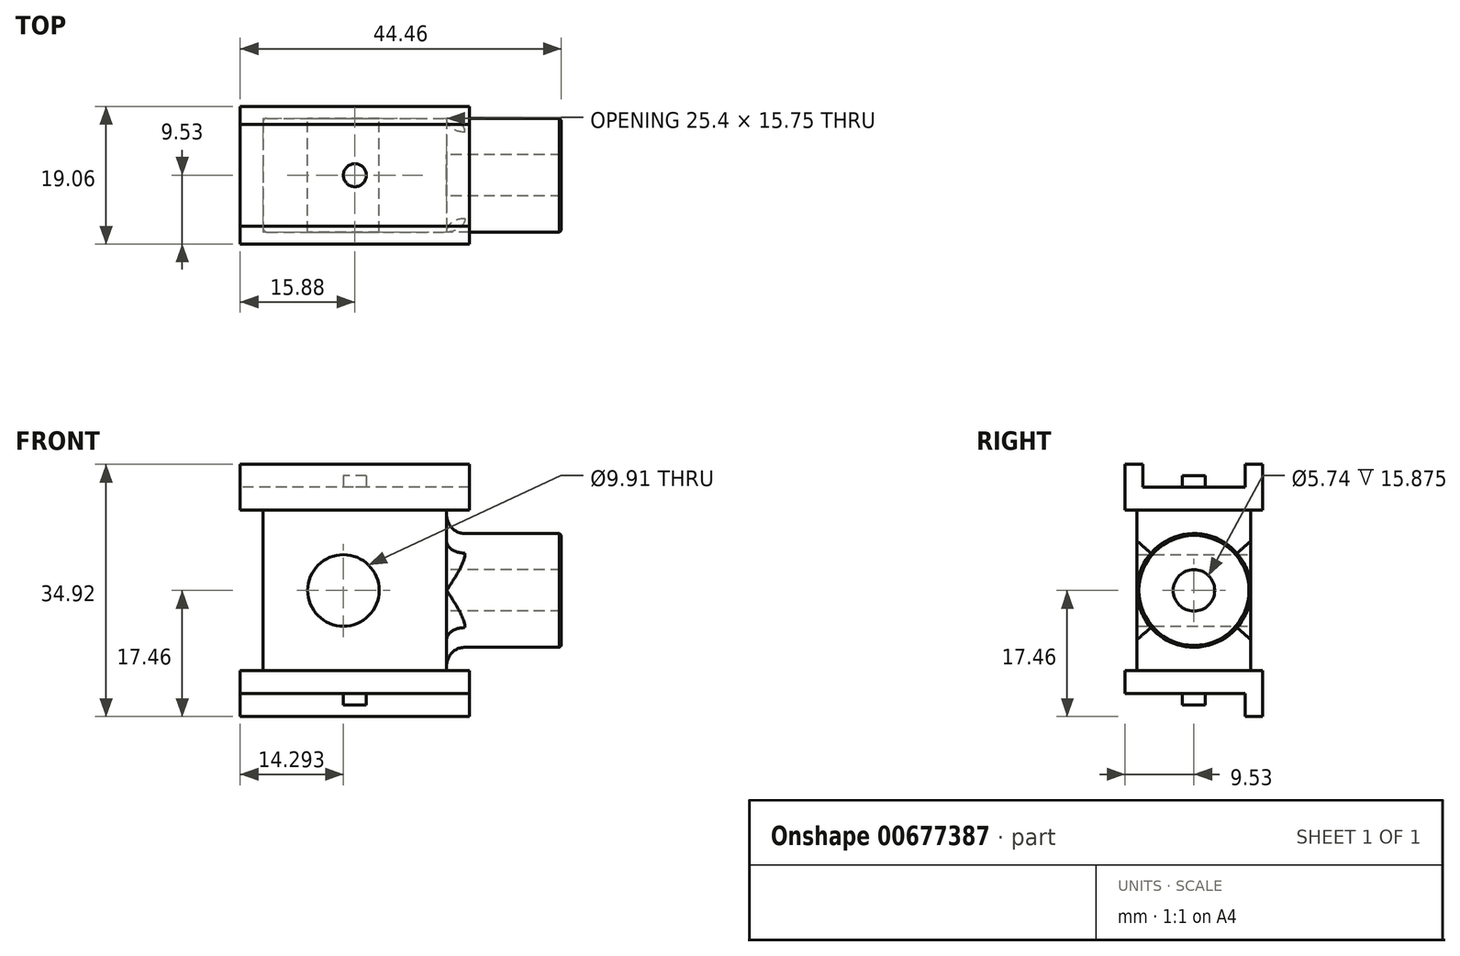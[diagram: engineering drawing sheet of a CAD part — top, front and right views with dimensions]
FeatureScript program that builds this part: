
annotation { "Feature Type Name" : "Feature", "Feature Type Description" : "" }
export const myFeature = defineFeature(function(context is Context, id is Id, definition is map)
    precondition{}
    {
        {
            var Q0;
            Q0=qCreatedBy(makeId("Top.planeOp"),FACE);
            var sketch = newSketch(context, id + "F0", { "sketchPlane" : qUnion([Q0])});
            skLineSegment(sketch, "E0.bottom", {"start": v(-12.7, 7.87) * mm, "end": v(12.7, 7.87) * mm});
            skLineSegment(sketch, "E0.top", {"start": v(-12.7, -7.87) * mm, "end": v(12.7, -7.87) * mm});
            skLineSegment(sketch, "E0.left", {"start": v(-12.7, 7.87) * mm, "end": v(-12.7, -7.87) * mm});
            skLineSegment(sketch, "E0.right", {"start": v(12.7, 7.87) * mm, "end": v(12.7, -7.87) * mm});
            skPoint(sketch, "E0.middle", {"position": v(0, 0) * mm});
            skSolve(sketch);
        }
        {
            var Q0;
            Q0=makeQuery(id+"F0.imprint","IMPRINT",FACE,{"disambiguationData":[TD([[makeQuery(id+"F0.imprint","IMPRINT",EDGE,{"derivedFrom":sQuery(id+"F0.wireOp",EDGE,"E0.bottom")}),-1.0]])]});
            extrude(context, id + "F1", {"entities" : qUnion([Q0]), "endBound" : BoundingType.SYMMETRIC, "depth" : 22.22 * mm, "offsetDistance" : 25.4 * mm});
        }
        {
            var Q0;
            Q0=makeQuery(id+"F1.opExtrude","CAP_FACE",FACE,{"disambiguationData":[OSD([sQuery(id+"F0.wireOp",EDGE,"E0.bottom"),sQuery(id+"F0.wireOp",EDGE,"E0.top"),sQuery(id+"F0.wireOp",EDGE,"E0.left"),sQuery(id+"F0.wireOp",EDGE,"E0.right")])],"isStart":false});
            var sketch = newSketch(context, id + "F2", { "sketchPlane" : qUnion([Q0])});
            skLineSegment(sketch, "E1.bottom", {"start": v(-15.87, 9.52) * mm, "end": v(15.88, 9.52) * mm});
            skLineSegment(sketch, "E1.top", {"start": v(-15.88, -9.52) * mm, "end": v(15.87, -9.52) * mm});
            skLineSegment(sketch, "E1.left", {"start": v(-15.88, 9.52) * mm, "end": v(-15.88, -9.52) * mm});
            skLineSegment(sketch, "E1.right", {"start": v(15.88, 9.52) * mm, "end": v(15.87, -9.52) * mm});
            skPoint(sketch, "E1.middle", {"position": v(0, 0) * mm});
            skSolve(sketch);
        }
        {
            var Q0;
            Q0=makeQuery(id+"F1.opExtrude","CAP_FACE",FACE,{"disambiguationData":[OSD([sQuery(id+"F0.wireOp",EDGE,"E0.bottom"),sQuery(id+"F0.wireOp",EDGE,"E0.top"),sQuery(id+"F0.wireOp",EDGE,"E0.left"),sQuery(id+"F0.wireOp",EDGE,"E0.right")])],"isStart":true});
            var sketch = newSketch(context, id + "F3", { "sketchPlane" : qUnion([Q0])});
            skLineSegment(sketch, "E2.bottom", {"start": v(15.88, -9.52) * mm, "end": v(-15.88, -9.53) * mm});
            skLineSegment(sketch, "E2.top", {"start": v(15.88, 9.53) * mm, "end": v(-15.88, 9.53) * mm});
            skLineSegment(sketch, "E2.left", {"start": v(15.88, -9.52) * mm, "end": v(15.87, 9.53) * mm});
            skLineSegment(sketch, "E2.right", {"start": v(-15.88, -9.53) * mm, "end": v(-15.88, 9.52) * mm});
            skPoint(sketch, "E2.middle", {"position": v(0, 0) * mm});
            skSolve(sketch);
        }
        {
            var Q0;
            Q0=makeQuery(id+"F2.imprint","IMPRINT",FACE,{"disambiguationData":[TD([[makeQuery(id+"F2.imprint","IMPRINT",EDGE,{"derivedFrom":makeQuery(id+"F1.opExtrude","CAP_EDGE",EDGE,{"disambiguationData":[OSD([sQuery(id+"F0.wireOp",EDGE,"E0.bottom")])],"isStart":false})}),-1.0]])]});
            var Q1;
            Q1=makeQuery(id+"F2.imprint","IMPRINT",FACE,{"disambiguationData":[TD([[makeQuery(id+"F2.imprint","IMPRINT",EDGE,{"derivedFrom":sQuery(id+"F2.wireOp",EDGE,"E1.bottom")}),-1.0]])]});
            extrude(context, id + "F4", {"entities" : qUnion([Q0, Q1]), "operationType" : NewBodyOperationType.ADD, "depth" : 3.17 * mm, "offsetDistance" : 25.4 * mm});
        }
        {
            var Q0;
            Q0=makeQuery(id+"F3.imprint","IMPRINT",FACE,{"disambiguationData":[TD([[makeQuery(id+"F3.imprint","IMPRINT",EDGE,{"derivedFrom":makeQuery(id+"F1.opExtrude","CAP_EDGE",EDGE,{"disambiguationData":[OSD([sQuery(id+"F0.wireOp",EDGE,"E0.bottom")])],"isStart":true})}),1.0]])]});
            var Q1;
            Q1=makeQuery(id+"F3.imprint","IMPRINT",FACE,{"disambiguationData":[TD([[makeQuery(id+"F3.imprint","IMPRINT",EDGE,{"derivedFrom":sQuery(id+"F3.wireOp",EDGE,"E2.bottom")}),-1.0]])]});
            extrude(context, id + "F5", {"entities" : qUnion([Q0, Q1]), "operationType" : NewBodyOperationType.ADD, "depth" : 3.17 * mm, "offsetDistance" : 25.4 * mm});
        }
        {
            var Q0;
            Q0=makeQuery(id+"F5.opExtrude","CAP_FACE",FACE,{"disambiguationData":[OSD([sQuery(id+"F3.wireOp",EDGE,"E2.bottom"),sQuery(id+"F3.wireOp",EDGE,"E2.top"),sQuery(id+"F3.wireOp",EDGE,"E2.left"),sQuery(id+"F3.wireOp",EDGE,"E2.right")])],"isStart":false});
            var sketch = newSketch(context, id + "F6", { "sketchPlane" : qUnion([Q0])});
            skLineSegment(sketch, "E3", {"start": v(-15.88, -9.53) * mm, "end": v(15.88, -9.52) * mm});
            skLineSegment(sketch, "E4", {"start": v(15.88, -9.52) * mm, "end": v(15.88, -7.06) * mm});
            skLineSegment(sketch, "E5", {"start": v(15.88, -7.06) * mm, "end": v(-15.88, -7.06) * mm});
            skLineSegment(sketch, "E6", {"start": v(-15.88, -7.06) * mm, "end": v(-15.88, -9.53) * mm});
            skLineSegment(sketch, "E7", {"start": v(-15.88, 9.52) * mm, "end": v(15.87, 9.53) * mm});
            skLineSegment(sketch, "E8", {"start": v(15.87, 9.53) * mm, "end": v(-15.88, 9.52) * mm});
            skLineSegment(sketch, "E9", {"start": v(-15.88, 7.06) * mm, "end": v(15.88, 7.06) * mm});
            skLineSegment(sketch, "E10", {"start": v(15.88, 7.06) * mm, "end": v(15.88, 9.53) * mm});
            skLineSegment(sketch, "E11", {"start": v(-15.88, 7.06) * mm, "end": v(-15.88, 9.52) * mm});
            skSolve(sketch);
        }
        {
            var Q0;
            Q0=makeQuery(id+"F6.imprint","IMPRINT",FACE,{"disambiguationData":[TD([[makeQuery(id+"F6.imprint","IMPRINT",EDGE,{"derivedFrom":sQuery(id+"F6.wireOp",EDGE,"E3")}),-1.0]])]});
            var Q1;
            Q1=makeQuery(id+"F6.imprint","IMPRINT",FACE,{"disambiguationData":[TD([[makeQuery(id+"F6.imprint","IMPRINT",EDGE,{"derivedFrom":sQuery(id+"F6.wireOp",EDGE,"E8")}),1.0]])]});
            extrude(context, id + "F7", {"entities" : qUnion([Q0, Q1]), "operationType" : NewBodyOperationType.ADD, "depth" : 3.17 * mm, "offsetDistance" : 25.4 * mm});
        }
        {
            var Q0;
            Q0=makeQuery(id+"F4.opExtrude","CAP_FACE",FACE,{"disambiguationData":[OSD([sQuery(id+"F2.wireOp",EDGE,"E1.bottom"),sQuery(id+"F2.wireOp",EDGE,"E1.top"),sQuery(id+"F2.wireOp",EDGE,"E1.left"),sQuery(id+"F2.wireOp",EDGE,"E1.right")])],"isStart":false});
            var sketch = newSketch(context, id + "F8", { "sketchPlane" : qUnion([Q0])});
            skLineSegment(sketch, "E12", {"start": v(15.87, -9.52) * mm, "end": v(-15.88, -9.52) * mm});
            skLineSegment(sketch, "E13", {"start": v(-15.88, -9.52) * mm, "end": v(-15.88, -7.06) * mm});
            skLineSegment(sketch, "E14", {"start": v(-15.88, -7.06) * mm, "end": v(15.87, -7.06) * mm});
            skLineSegment(sketch, "E15", {"start": v(15.88, -7.06) * mm, "end": v(15.88, -9.52) * mm});
            skLineSegment(sketch, "E16", {"start": v(15.88, 9.52) * mm, "end": v(15.88, 7.06) * mm});
            skLineSegment(sketch, "E17", {"start": v(15.88, 7.06) * mm, "end": v(-15.88, 7.06) * mm});
            skLineSegment(sketch, "E18", {"start": v(-15.88, 7.06) * mm, "end": v(-15.88, 9.52) * mm});
            skLineSegment(sketch, "E19", {"start": v(-15.88, 9.52) * mm, "end": v(15.88, 9.52) * mm});
            skSolve(sketch);
        }
        {
            var Q0;
            Q0=makeQuery(id+"F8.imprint","IMPRINT",FACE,{"disambiguationData":[TD([[makeQuery(id+"F8.imprint","IMPRINT",EDGE,{"derivedFrom":sQuery(id+"F8.wireOp",EDGE,"E12")}),1.0]])]});
            var Q1;
            Q1=makeQuery(id+"F8.imprint","IMPRINT",FACE,{"disambiguationData":[TD([[makeQuery(id+"F8.imprint","IMPRINT",EDGE,{"derivedFrom":sQuery(id+"F8.wireOp",EDGE,"E16")}),-1.0]])]});
            extrude(context, id + "F9", {"entities" : qUnion([Q0, Q1]), "operationType" : NewBodyOperationType.ADD, "depth" : 3.17 * mm, "offsetDistance" : 25.4 * mm});
        }
        {
            var Q0;
            Q0=makeQuery(id+"F1.opExtrude","SWEPT_FACE",FACE,{"disambiguationData":[OSD([sQuery(id+"F0.wireOp",EDGE,"E0.right")])]});
            var sketch = newSketch(context, id + "F10", { "sketchPlane" : qUnion([Q0])});
            skCircle(sketch, "E20", {"center": v(0, 0) * mm, "radius": 7.87 * mm});
            skCircle(sketch, "E21", {"center": v(0, 0) * mm, "radius": 2.87 * mm});
            skSolve(sketch);
        }
        {
            var Q0;
            Q0=makeQuery(id+"F10.imprint","IMPRINT",FACE,{"disambiguationData":[TD([[makeQuery(id+"F10.imprint","IMPRINT",EDGE,{"derivedFrom":sQuery(id+"F10.wireOp",EDGE,"E21")}),-1.0]])]});
            extrude(context, id + "F11", {"entities" : qUnion([Q0]), "operationType" : NewBodyOperationType.ADD, "depth" : 15.88 * mm, "offsetDistance" : 25.4 * mm});
        }
        {
            var Q0;
            Q0=makeQuery(id+"F1.opExtrude","SWEPT_FACE",FACE,{"disambiguationData":[OSD([sQuery(id+"F0.wireOp",EDGE,"E0.bottom")])]});
            var sketch = newSketch(context, id + "F12", { "sketchPlane" : qUnion([Q0])});
            skCircle(sketch, "E22", {"center": v(1.59, 0) * mm, "radius": 4.95 * mm});
            skSolve(sketch);
        }
        {
            var Q0;
            Q0=makeQuery(id+"F12.imprint","IMPRINT",FACE,{"disambiguationData":[TD([[makeQuery(id+"F12.imprint","IMPRINT",EDGE,{"derivedFrom":sQuery(id+"F12.wireOp",EDGE,"E22")}),1.0]])]});
            extrude(context, id + "F13", {"entities" : qUnion([Q0]), "operationType" : NewBodyOperationType.REMOVE, "endBound" : BoundingType.THROUGH_ALL, "oppositeDirection" : true, "depth" : 25.4 * mm, "offsetDistance" : 25.4 * mm});
        }
        {
            var Q0;
            Q0=makeQuery(id+"F4.opExtrude","CAP_FACE",FACE,{"disambiguationData":[OSD([sQuery(id+"F2.wireOp",EDGE,"E1.bottom"),sQuery(id+"F2.wireOp",EDGE,"E1.top"),sQuery(id+"F2.wireOp",EDGE,"E1.left"),sQuery(id+"F2.wireOp",EDGE,"E1.right")])],"isStart":false});
            var sketch = newSketch(context, id + "F14", { "sketchPlane" : qUnion([Q0])});
            skCircle(sketch, "E23", {"center": v(0, 0) * mm, "radius": 1.59 * mm});
            skSolve(sketch);
        }
        {
            var Q0;
            Q0=makeQuery(id+"F14.imprint","IMPRINT",FACE,{"disambiguationData":[TD([[makeQuery(id+"F14.imprint","IMPRINT",EDGE,{"derivedFrom":sQuery(id+"F14.wireOp",EDGE,"E23")}),1.0]])]});
            extrude(context, id + "F15", {"entities" : qUnion([Q0]), "operationType" : NewBodyOperationType.ADD, "depth" : 1.59 * mm, "offsetDistance" : 25.4 * mm});
        }
        {
            var Q0;
            Q0=makeQuery(id+"F5.opExtrude","CAP_FACE",FACE,{"disambiguationData":[OSD([sQuery(id+"F3.wireOp",EDGE,"E2.bottom"),sQuery(id+"F3.wireOp",EDGE,"E2.top"),sQuery(id+"F3.wireOp",EDGE,"E2.left"),sQuery(id+"F3.wireOp",EDGE,"E2.right")])],"isStart":false});
            var sketch = newSketch(context, id + "F16", { "sketchPlane" : qUnion([Q0])});
            skCircle(sketch, "E24", {"center": v(0, 0) * mm, "radius": 1.59 * mm});
            skSolve(sketch);
        }
        {
            var Q0;
            Q0=makeQuery(id+"F16.imprint","IMPRINT",FACE,{"disambiguationData":[TD([[makeQuery(id+"F16.imprint","IMPRINT",EDGE,{"derivedFrom":sQuery(id+"F16.wireOp",EDGE,"E24")}),1.0]])]});
            extrude(context, id + "F17", {"entities" : qUnion([Q0]), "operationType" : NewBodyOperationType.ADD, "depth" : 1.59 * mm, "offsetDistance" : 25.4 * mm});
        }
        {
            var Q0;
            Q0=makeQuery(id+"F11.boolean.opBoolean","SPLIT",EDGE,{"disambiguationData":[OD(0.0)],"derivedFrom":makeQuery(id+"F11.opExtrude","CAP_EDGE",EDGE,{"disambiguationData":[OSD([sQuery(id+"F10.wireOp",EDGE,"E20")])],"isStart":true})});
            fillet(context, id + "F18", {"entities" : qUnion([Q0]), "radius" : 2.54 * mm, "tangentPropagation" : true, "allowEdgeOverflow" : false});
        }
        {
            var Q0;
            Q0=makeQuery(id+"F1.opExtrude","CAP_EDGE",EDGE,{"disambiguationData":[OSD([sQuery(id+"F0.wireOp",EDGE,"E0.bottom")])],"isStart":false});
            var Q1;
            Q1=makeQuery(id+"F1.opExtrude","CAP_EDGE",EDGE,{"disambiguationData":[OSD([sQuery(id+"F0.wireOp",EDGE,"E0.right")])],"isStart":false});
            var Q2;
            Q2=makeQuery(id+"F1.opExtrude","CAP_EDGE",EDGE,{"disambiguationData":[OSD([sQuery(id+"F0.wireOp",EDGE,"E0.bottom")])],"isStart":true});
            var Q3;
            Q3=makeQuery(id+"F1.opExtrude","CAP_EDGE",EDGE,{"disambiguationData":[OSD([sQuery(id+"F0.wireOp",EDGE,"E0.left")])],"isStart":false});
            var Q4;
            Q4=makeQuery(id+"F1.opExtrude","CAP_EDGE",EDGE,{"disambiguationData":[OSD([sQuery(id+"F0.wireOp",EDGE,"E0.left")])],"isStart":true});
            var Q5;
            Q5=makeQuery(id+"F1.opExtrude","CAP_EDGE",EDGE,{"disambiguationData":[OSD([sQuery(id+"F0.wireOp",EDGE,"E0.top")])],"isStart":true});
            var Q6;
            Q6=makeQuery(id+"F1.opExtrude","CAP_EDGE",EDGE,{"disambiguationData":[OSD([sQuery(id+"F0.wireOp",EDGE,"E0.right")])],"isStart":true});
            var Q7;
            Q7=makeQuery(id+"F1.opExtrude","CAP_EDGE",EDGE,{"disambiguationData":[OSD([sQuery(id+"F0.wireOp",EDGE,"E0.top")])],"isStart":false});
            var Q8;
            Q8=makeQuery(id+"F1.opExtrude","SWEPT_EDGE",EDGE,{"disambiguationData":[OSD([sQuery(id+"F0.wireOp",EDGE,"E0.top"),sQuery(id+"F0.wireOp",EDGE,"E0.left")])]});
            var Q9;
            Q9=makeQuery(id+"F1.opExtrude","SWEPT_EDGE",EDGE,{"disambiguationData":[OSD([sQuery(id+"F0.wireOp",EDGE,"E0.bottom"),sQuery(id+"F0.wireOp",EDGE,"E0.left")])]});
            fillet(context, id + "F19", {"entities" : qUnion([Q0, Q1, Q2, Q3, Q4, Q5, Q6, Q7, Q8, Q9]), "radius" : 0.5 * mm, "tangentPropagation" : true, "allowEdgeOverflow" : false});
        }
        {
            var Q0;
            Q0=makeQuery(id+"F11.opExtrude","CAP_EDGE",EDGE,{"disambiguationData":[OSD([sQuery(id+"F10.wireOp",EDGE,"E20")])],"isStart":false});
            chamfer(context, id + "F20", {"entities" : qUnion([Q0]), "width" : 0.25 * mm, "tangentPropagation" : true});
        }
    });
